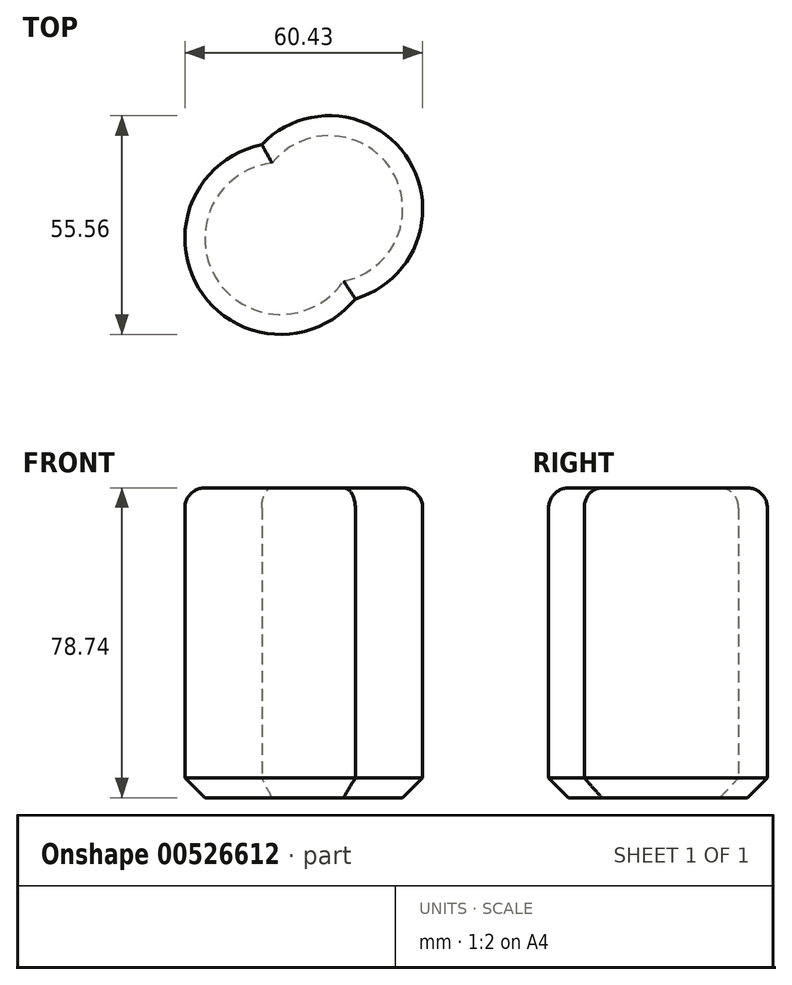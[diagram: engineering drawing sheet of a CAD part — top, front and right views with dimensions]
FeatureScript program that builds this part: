
annotation { "Feature Type Name" : "Feature", "Feature Type Description" : "" }
export const myFeature = defineFeature(function(context is Context, id is Id, definition is map)
    precondition{}
    {
        {
            var Q0;
            Q0=qCreatedBy(makeId("Top.planeOp"),FACE);
            var sketch = newSketch(context, id + "F0", { "sketchPlane" : qUnion([Q0])});
            skArc(sketch, "E0", {"start": v(0, 0) * mm, "mid": v(13.7, 35.08) * mm, "end": v(-23.74, 39.2) * mm});
            skArc(sketch, "E1", {"start": v(-23.74, 39.2) * mm, "mid": v(-39.78, 2.7) * mm, "end": v(0, 0) * mm});
            skSolve(sketch);
        }
        {
            var Q0;
            Q0=makeQuery(id+"F0.imprint","IMPRINT",FACE,{"disambiguationData":[TD([[makeQuery(id+"F0.imprint","IMPRINT",EDGE,{"derivedFrom":sQuery(id+"F0.wireOp",EDGE,"E0")}),1.0]])]});
            extrude(context, id + "F1", {"entities" : qUnion([Q0]), "depth" : 78.74 * mm, "offsetDistance" : 25.4 * mm});
        }
        {
            var Q0;
            Q0=makeQuery(id+"F1.opExtrude","CAP_EDGE",EDGE,{"disambiguationData":[OSD([sQuery(id+"F0.wireOp",EDGE,"E1")])],"isStart":false});
            var Q1;
            Q1=makeQuery(id+"F1.opExtrude","CAP_EDGE",EDGE,{"disambiguationData":[OSD([sQuery(id+"F0.wireOp",EDGE,"E0")])],"isStart":false});
            fillet(context, id + "F2", {"entities" : qUnion([Q0, Q1]), "radius" : 5.08 * mm, "tangentPropagation" : true, "allowEdgeOverflow" : false});
        }
        {
            var Q0;
            Q0=makeQuery(id+"F1.opExtrude","CAP_FACE",FACE,{"disambiguationData":[OSD([sQuery(id+"F0.wireOp",EDGE,"E0"),sQuery(id+"F0.wireOp",EDGE,"E1")])],"isStart":true});
            chamfer(context, id + "F3", {"entities" : qUnion([Q0]), "width" : 5.08 * mm, "tangentPropagation" : true});
        }
    });
